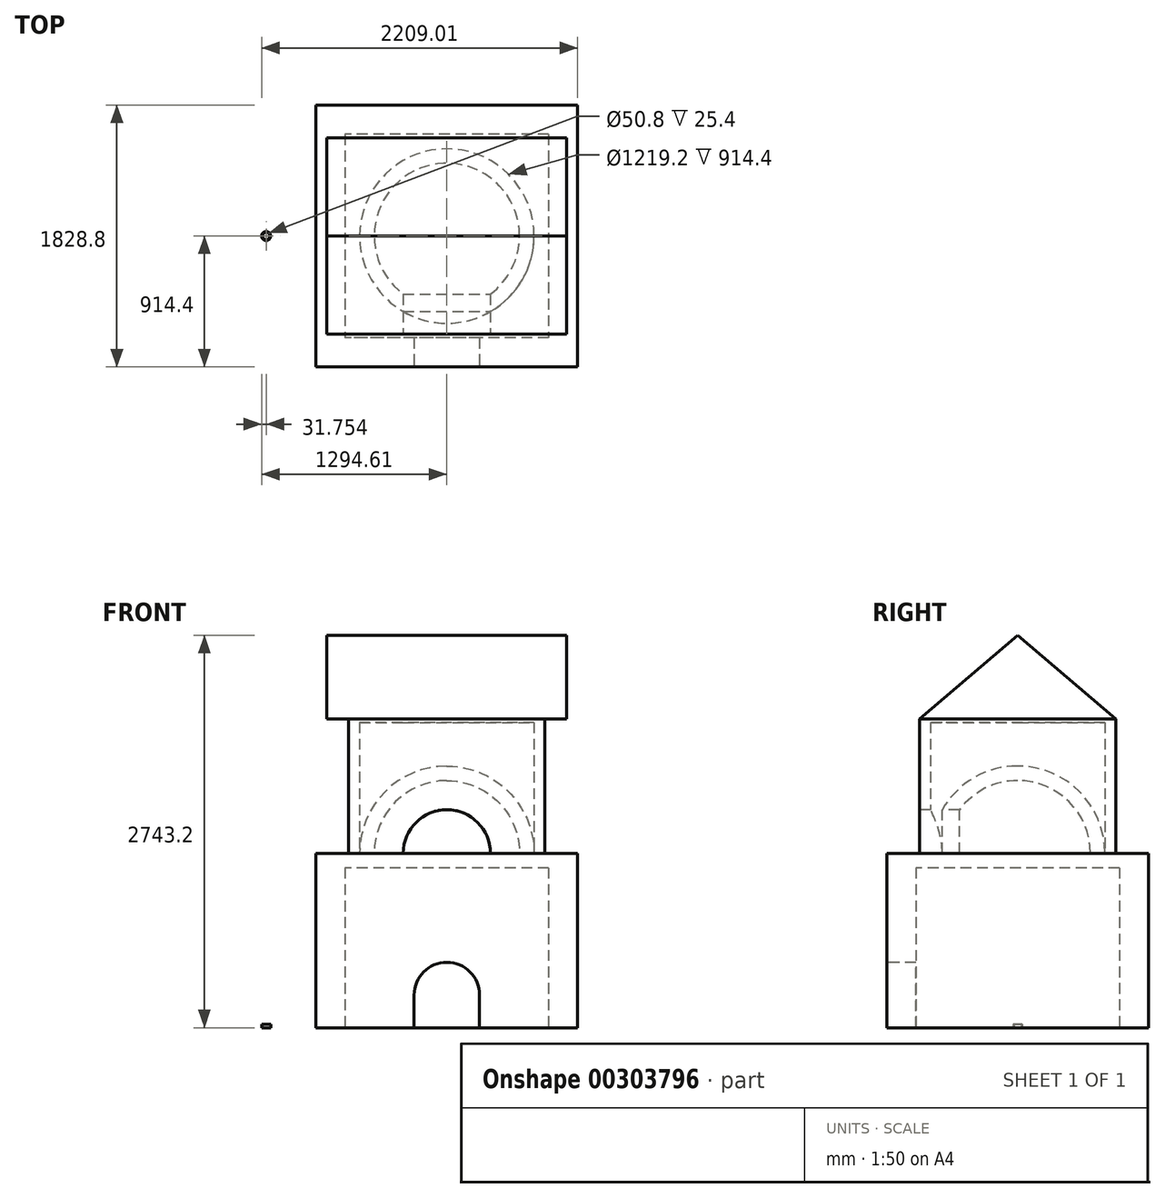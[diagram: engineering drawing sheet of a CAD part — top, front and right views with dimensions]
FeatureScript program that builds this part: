
annotation { "Feature Type Name" : "Feature", "Feature Type Description" : "" }
export const myFeature = defineFeature(function(context is Context, id is Id, definition is map)
    precondition{}
    {
        {
            var Q0;
            Q0=qCreatedBy(makeId("Top.planeOp"),FACE);
            var sketch = newSketch(context, id + "F0", { "sketchPlane" : qUnion([Q0])});
            skLineSegment(sketch, "E0.bottom", {"start": v(-914.4, 914.4) * mm, "end": v(914.4, 914.4) * mm});
            skLineSegment(sketch, "E0.top", {"start": v(-914.4, -914.4) * mm, "end": v(914.4, -914.4) * mm});
            skLineSegment(sketch, "E0.left", {"start": v(-914.4, 914.4) * mm, "end": v(-914.4, -914.4) * mm});
            skLineSegment(sketch, "E0.right", {"start": v(914.4, 914.4) * mm, "end": v(914.4, -914.4) * mm});
            skPoint(sketch, "E0.middle", {"position": v(0, 0) * mm});
            skLineSegment(sketch, "E1.bottom", {"start": v(711.2, 711.2) * mm, "end": v(-711.2, 711.2) * mm});
            skLineSegment(sketch, "E1.top", {"start": v(711.2, -711.2) * mm, "end": v(-711.2, -711.2) * mm});
            skLineSegment(sketch, "E1.left", {"start": v(711.2, 711.2) * mm, "end": v(711.2, -711.2) * mm});
            skLineSegment(sketch, "E1.right", {"start": v(-711.2, 711.2) * mm, "end": v(-711.2, -711.2) * mm});
            skSolve(sketch);
        }
        {
            var Q0;
            Q0 = qSketchRegion(id + "F0", true);
            extrude(context, id + "F1", {"entities" : qUnion([Q0]), "depth" : 1219.2 * mm});
        }
        {
            var Q0;
            Q0=makeQuery(id+"F1.opExtrude","CAP_FACE",FACE,{"disambiguationData":[OSD([sQuery(id+"F0.wireOp",EDGE,"E0.bottom"),sQuery(id+"F0.wireOp",EDGE,"E0.top"),sQuery(id+"F0.wireOp",EDGE,"E0.left"),sQuery(id+"F0.wireOp",EDGE,"E0.right")])],"isStart":false});
            var sketch = newSketch(context, id + "F2", { "sketchPlane" : qUnion([Q0])});
            skCircle(sketch, "E2", {"center": v(0, 0) * mm, "radius": 609.6 * mm});
            skLineSegment(sketch, "E3.bottom", {"start": v(685.8, 685.8) * mm, "end": v(-685.8, 685.8) * mm});
            skLineSegment(sketch, "E3.top", {"start": v(685.8, -685.8) * mm, "end": v(-685.8, -685.8) * mm});
            skLineSegment(sketch, "E3.left", {"start": v(685.8, 685.8) * mm, "end": v(685.8, -685.8) * mm});
            skLineSegment(sketch, "E3.right", {"start": v(-685.8, 685.8) * mm, "end": v(-685.8, -685.8) * mm});
            skSolve(sketch);
        }
        {
            var Q0;
            Q0=qCreatedBy(makeId("Front.planeOp"),FACE);
            var sketch = newSketch(context, id + "F3", { "sketchPlane" : qUnion([Q0])});
            skArc(sketch, "E4", {"start": v(609.6, 1219.2) * mm, "mid": v(431.05, 1650.25) * mm, "end": v(0, 1828.8) * mm});
            skLineSegment(sketch, "E5", {"start": v(-920.2, 1219.2) * mm, "end": v(910.09, 1219.2) * mm});
            skLineSegment(sketch, "E6", {"start": v(0, 1219.2) * mm, "end": v(0, 1828.8) * mm});
            skPoint(sketch, "E6.endSnap0", {"position": v(0, 1828.8) * mm});
            skArc(sketch, "E7.0", {"start": v(508, 1219.2) * mm, "mid": v(359.21, 1578.41) * mm, "end": v(0, 1727.2) * mm});
            skSolve(sketch);
        }
        {
            var Q0;
            {var subQ0=sQuery(id+"F3.wireOp",EDGE,"E4");Q0=makeQuery(id+"F3.imprint","IMPRINT",FACE,{"disambiguationData":[TD([[makeQuery(id+"F3.imprint","IMPRINT",EDGE,{"derivedFrom":subQ0}),1.0]])]});}
            var Q1;
            Q1=sQuery(id+"F3.wireOp",EDGE,"E6");
            revolve(context, id + "F4", {"operationType" : NewBodyOperationType.ADD, "entities" : qUnion([Q0]), "axis" : qUnion([Q1]), "revolveType" : RevolveType.FULL});
        }
        {
            var Q0;
            Q0=makeQuery(id+"F2.imprint","IMPRINT",FACE,{"disambiguationData":[TD([[makeQuery(id+"F2.imprint","IMPRINT",EDGE,{"derivedFrom":sQuery(id+"F2.wireOp",EDGE,"E2")}),-1.0]])]});
            var Q1;
            Q1=sQuery(id+"F2.wireOp",EDGE,"E3.left");
            var Q2;
            Q2=sQuery(id+"F2.wireOp",EDGE,"E3.top");
            var Q3;
            Q3=sQuery(id+"F2.wireOp",EDGE,"E3.right");
            var Q4;
            Q4=sQuery(id+"F2.wireOp",EDGE,"E3.bottom");
            var Q5;
            Q5=makeQuery(id+"F1.opExtrude","SWEPT_BODY",BODY,{"disambiguationData":[OSD([sQuery(id+"F0.wireOp",EDGE,"E0.bottom"),sQuery(id+"F0.wireOp",EDGE,"E0.top"),sQuery(id+"F0.wireOp",EDGE,"E0.left"),sQuery(id+"F0.wireOp",EDGE,"E0.right")])]});
            extrude(context, id + "F5", {"entities" : qUnion([Q0]), "surfaceEntities" : qUnion([Q1, Q2, Q3, Q4]), "endBoundEntityBody" : qUnion([Q5]), "depth" : 914.4 * mm});
        }
        {
            var Q0;
            Q0=makeQuery(id+"F5.opExtrude","CAP_FACE",FACE,{"disambiguationData":[OSD([sQuery(id+"F2.wireOp",EDGE,"E2"),sQuery(id+"F2.wireOp",EDGE,"E3.bottom"),sQuery(id+"F2.wireOp",EDGE,"E3.top"),sQuery(id+"F2.wireOp",EDGE,"E3.left"),sQuery(id+"F2.wireOp",EDGE,"E3.right")])],"isStart":false});
            var sketch = newSketch(context, id + "F6", { "sketchPlane" : qUnion([Q0])});
            skLineSegment(sketch, "E8.bottom", {"start": v(685.8, 685.8) * mm, "end": v(-685.8, 685.8) * mm});
            skLineSegment(sketch, "E8.top", {"start": v(685.8, -685.8) * mm, "end": v(-685.8, -685.8) * mm});
            skLineSegment(sketch, "E8.left", {"start": v(685.8, 685.8) * mm, "end": v(685.8, -685.8) * mm});
            skLineSegment(sketch, "E8.right", {"start": v(-685.8, 685.8) * mm, "end": v(-685.8, -685.8) * mm});
            skPoint(sketch, "E8.middle", {"position": v(0, 0) * mm});
            skSolve(sketch);
        }
        {
            var Q0;
            Q0 = qSketchRegion(id + "F6", true);
            extrude(context, id + "F7", {"entities" : qUnion([Q0]), "operationType" : NewBodyOperationType.ADD, "depth" : 25.4 * mm});
        }
        {
            var Q0;
            Q0=makeQuery(id+"F1.opExtrude","SWEPT_FACE",FACE,{"disambiguationData":[OSD([sQuery(id+"F0.wireOp",EDGE,"E0.top")])]});
            var sketch = newSketch(context, id + "F8", { "sketchPlane" : qUnion([Q0])});
            skPoint(sketch, "E9.endSnap0", {"position": v(0, 1219.2) * mm});
            skArc(sketch, "E10", {"start": v(228.6, 228.6) * mm, "mid": v(0, 457.2) * mm, "end": v(-228.6, 228.6) * mm});
            skLineSegment(sketch, "E11", {"start": v(-228.6, 228.6) * mm, "end": v(-228.6, 0) * mm});
            skLineSegment(sketch, "E12", {"start": v(-228.6, 0) * mm, "end": v(228.6, 0) * mm});
            skLineSegment(sketch, "E13", {"start": v(228.6, 0) * mm, "end": v(228.6, 228.6) * mm});
            skSolve(sketch);
        }
        {
            var Q0;
            Q0=makeQuery(id+"F2.imprint","IMPRINT",FACE,{"disambiguationData":[TD([[makeQuery(id+"F2.imprint","IMPRINT",EDGE,{"derivedFrom":makeQuery(id+"F1.opExtrude","CAP_EDGE",EDGE,{"disambiguationData":[OSD([sQuery(id+"F0.wireOp",EDGE,"E0.bottom")])],"isStart":false})}),-1.0]])]});
            var sketch = newSketch(context, id + "F9", { "sketchPlane" : qUnion([Q0])});
            skLineSegment(sketch, "E14.bottom", {"start": v(711.2, 711.2) * mm, "end": v(-711.2, 711.2) * mm});
            skLineSegment(sketch, "E14.top", {"start": v(711.2, -711.2) * mm, "end": v(-711.2, -711.2) * mm});
            skLineSegment(sketch, "E14.left", {"start": v(711.2, 711.2) * mm, "end": v(711.2, -711.2) * mm});
            skLineSegment(sketch, "E14.right", {"start": v(-711.2, 711.2) * mm, "end": v(-711.2, -711.2) * mm});
            skPoint(sketch, "E14.middle", {"position": v(0, 0) * mm});
            skSolve(sketch);
        }
        {
            var Q0;
            Q0 = qSketchRegion(id + "F9", true);
            extrude(context, id + "F10", {"entities" : qUnion([Q0]), "operationType" : NewBodyOperationType.ADD, "oppositeDirection" : true, "depth" : 101.6 * mm});
        }
        {
            var Q0;
            Q0 = qSketchRegion(id + "F8", true);
            extrude(context, id + "F11", {"entities" : qUnion([Q0]), "operationType" : NewBodyOperationType.REMOVE, "endBound" : BoundingType.UP_TO_NEXT, "oppositeDirection" : true, "depth" : 25.4 * mm});
        }
        {
            var Q0;
            Q0=makeQuery(id+"F7.boolean.opBoolean","MERGE",FACE,{"derivedFrom":[makeQuery(id+"F5.opExtrude","SWEPT_FACE",FACE,{"disambiguationData":[OSD([sQuery(id+"F2.wireOp",EDGE,"E3.left")])]}),makeQuery(id+"F7.opExtrude","SWEPT_FACE",FACE,{"disambiguationData":[OSD([sQuery(id+"F6.wireOp",EDGE,"E8.left")])]})]});
            var sketch = newSketch(context, id + "F12", { "sketchPlane" : qUnion([Q0])});
            skLineSegment(sketch, "E15", {"start": v(-685.8, 2159) * mm, "end": v(0, 2743.2) * mm});
            skLineSegment(sketch, "E16", {"start": v(0, 2743.2) * mm, "end": v(685.8, 2159) * mm});
            skLineSegment(sketch, "E17", {"start": v(685.8, 2159) * mm, "end": v(-685.8, 2159) * mm});
            skSolve(sketch);
        }
        {
            var Q0;
            Q0 = qSketchRegion(id + "F12", true);
            extrude(context, id + "F13", {"entities" : qUnion([Q0]), "operationType" : NewBodyOperationType.ADD, "oppositeDirection" : true, "depth" : 1524 * mm, "hasSecondDirection" : true, "secondDirectionOppositeDirection" : false, "secondDirectionDepth" : 152.4 * mm});
        }
        {
            var Q0;
            Q0=makeQuery(id+"F7.boolean.opBoolean","MERGE",FACE,{"derivedFrom":[makeQuery(id+"F5.opExtrude","SWEPT_FACE",FACE,{"disambiguationData":[OSD([sQuery(id+"F2.wireOp",EDGE,"E3.top")])]}),makeQuery(id+"F7.opExtrude","SWEPT_FACE",FACE,{"disambiguationData":[OSD([sQuery(id+"F6.wireOp",EDGE,"E8.top")])]})]});
            var sketch = newSketch(context, id + "F14", { "sketchPlane" : qUnion([Q0])});
            skArc(sketch, "E18", {"start": v(304.8, 1219.2) * mm, "mid": v(0, 1524) * mm, "end": v(-304.8, 1219.2) * mm});
            skLineSegment(sketch, "E19", {"start": v(-304.8, 1219.2) * mm, "end": v(304.8, 1219.2) * mm});
            skSolve(sketch);
        }
        {
            var Q0;
            Q0 = qSketchRegion(id + "F14", true);
            extrude(context, id + "F15", {"entities" : qUnion([Q0]), "operationType" : NewBodyOperationType.REMOVE, "oppositeDirection" : true, "depth" : 304.8 * mm, "hasSecondDirection" : true, "secondDirectionBound" : SecondDirectionBoundingType.THROUGH_ALL, "secondDirectionOppositeDirection" : false, "secondDirectionDepth" : 25.4 * mm});
        }
        {
            var Q0;
            Q0=makeQuery(id+"F1.opExtrude","CAP_FACE",FACE,{"disambiguationData":[OSD([sQuery(id+"F0.wireOp",EDGE,"E0.bottom"),sQuery(id+"F0.wireOp",EDGE,"E0.top"),sQuery(id+"F0.wireOp",EDGE,"E0.left"),sQuery(id+"F0.wireOp",EDGE,"E0.right"),sQuery(id+"F0.wireOp",EDGE,"E1.bottom"),sQuery(id+"F0.wireOp",EDGE,"E1.top"),sQuery(id+"F0.wireOp",EDGE,"E1.left"),sQuery(id+"F0.wireOp",EDGE,"E1.right")])],"isStart":true});
            var sketch = newSketch(context, id + "F16", { "sketchPlane" : qUnion([Q0])});
            skCircle(sketch, "E20", {"center": v(-1262.86, 0) * mm, "radius": 25.4 * mm});
            skPoint(sketch, "E20.centerSnap0", {"position": v(-711.2, 0) * mm});
            skCircle(sketch, "E21", {"center": v(-1262.86, 0) * mm, "radius": 31.75 * mm});
            skSolve(sketch);
        }
        {
            var Q0;
            Q0=makeQuery(id+"F16.imprint","IMPRINT",FACE,{"disambiguationData":[TD([[makeQuery(id+"F16.imprint","IMPRINT",EDGE,{"derivedFrom":sQuery(id+"F16.wireOp",EDGE,"E20")}),-1.0]])]});
            var Q1;
            Q1=sQuery(id+"F16.wireOp",EDGE,"E20");
            var Q2;
            Q2=sQuery(id+"F16.wireOp",EDGE,"E21");
            extrude(context, id + "F17", {"entities" : qUnion([Q0]), "surfaceEntities" : qUnion([Q1, Q2]), "oppositeDirection" : true, "depth" : 25.4 * mm});
        }
    });
